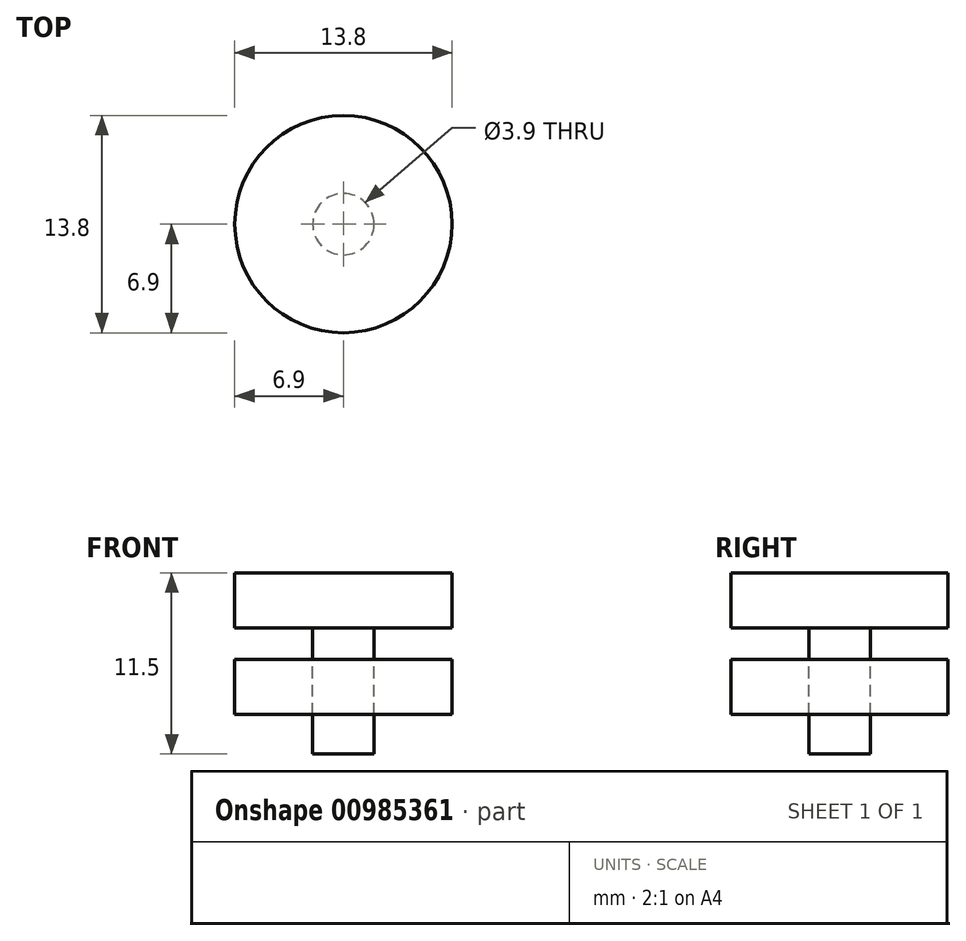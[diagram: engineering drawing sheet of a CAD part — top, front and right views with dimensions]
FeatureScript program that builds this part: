
annotation { "Feature Type Name" : "Feature", "Feature Type Description" : "" }
export const myFeature = defineFeature(function(context is Context, id is Id, definition is map)
    precondition{}
    {
        {
            var Q0;
            Q0=qCreatedBy(makeId("Top.planeOp"),FACE);
            var sketch = newSketch(context, id + "F0", { "sketchPlane" : qUnion([Q0])});
            skCircle(sketch, "E0", {"center": v(0, 0) * mm, "radius": 6.9 * mm});
            skCircle(sketch, "E1", {"center": v(0, 0) * mm, "radius": 1.95 * mm});
            skSolve(sketch);
        }
        {
            var Q0;
            Q0=makeQuery(id+"F0.imprint","IMPRINT",FACE,{"disambiguationData":[TD([[makeQuery(id+"F0.imprint","IMPRINT",EDGE,{"derivedFrom":sQuery(id+"F0.wireOp",EDGE,"E0")}),1.0]])]});
            var Q1;
            Q1=makeQuery(id+"F0.imprint","IMPRINT",FACE,{"disambiguationData":[TD([[makeQuery(id+"F0.imprint","IMPRINT",EDGE,{"derivedFrom":sQuery(id+"F0.wireOp",EDGE,"E1")}),1.0]])]});
            extrude(context, id + "F1", {"entities" : qUnion([Q0, Q1]), "depth" : 3.5 * mm, "offsetDistance" : 25 * mm});
        }
        {
            var Q0;
            Q0=makeQuery(id+"F0.imprint","IMPRINT",FACE,{"disambiguationData":[TD([[makeQuery(id+"F0.imprint","IMPRINT",EDGE,{"derivedFrom":sQuery(id+"F0.wireOp",EDGE,"E1")}),1.0]])]});
            var Q1;
            Q1=sQuery(id+"F0.wireOp",EDGE,"E1");
            extrude(context, id + "F2", {"entities" : qUnion([Q0]), "operationType" : NewBodyOperationType.ADD, "surfaceOperationType" : NewSurfaceOperationType.ADD, "surfaceEntities" : qUnion([Q1]), "depth" : -8 * mm, "offsetDistance" : 25 * mm});
        }
        {
            var Q0;
            Q0=makeQuery(id+"F1.opExtrude","SWEPT_BODY",BODY,{"disambiguationData":[OSD([sQuery(id+"F0.wireOp",EDGE,"E0")])]});
            transform(context, id + "F3", {"entities" : qUnion([Q0]), "transformType" : TransformType.TRANSLATION_3D, "dx" : 0 * mm, "dy" : 0 * mm, "dz" : 2 * mm, "makeCopy" : false});
        }
        {
            var Q0;
            Q0=makeQuery(id+"F0.imprint","IMPRINT",FACE,{"disambiguationData":[TD([[makeQuery(id+"F0.imprint","IMPRINT",EDGE,{"derivedFrom":sQuery(id+"F0.wireOp",EDGE,"E0")}),1.0]])]});
            extrude(context, id + "F4", {"entities" : qUnion([Q0]), "depth" : -3.5 * mm, "offsetDistance" : 25 * mm});
        }
    });
